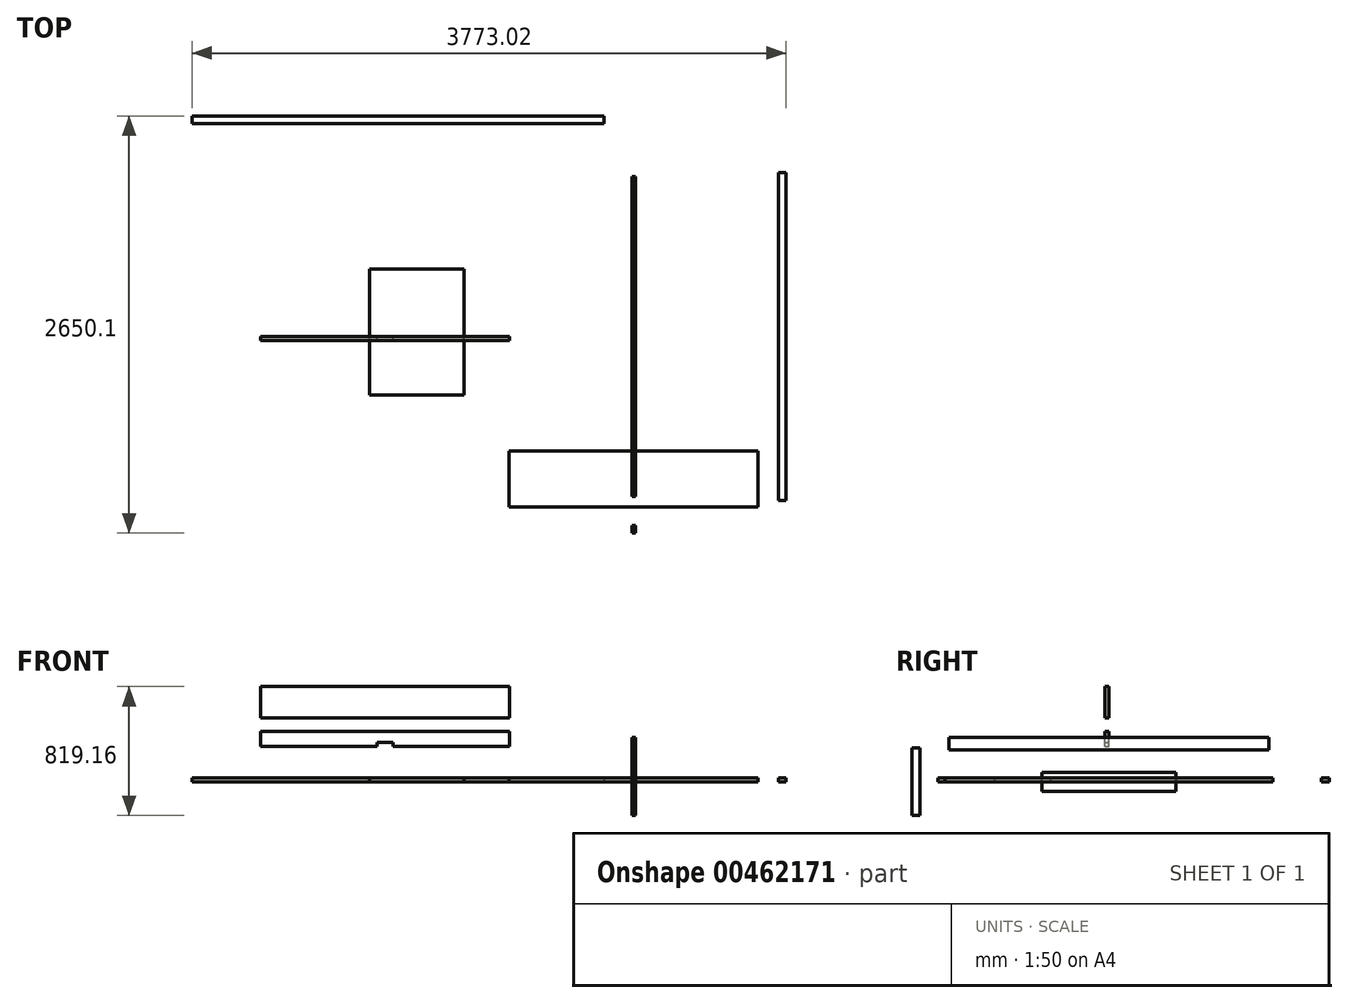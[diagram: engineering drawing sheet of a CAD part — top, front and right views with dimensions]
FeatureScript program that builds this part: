
annotation { "Feature Type Name" : "Feature", "Feature Type Description" : "" }
export const myFeature = defineFeature(function(context is Context, id is Id, definition is map)
    precondition{}
    {
        {
            var Q0;
            Q0=qCreatedBy(makeId("Right.planeOp"),FACE);
            var sketch = newSketch(context, id + "F0", { "sketchPlane" : qUnion([Q0])});
            skLineSegment(sketch, "E0", {"start": v(-1409.76, 0) * mm, "end": v(1225.16, 0) * mm, "construction": true});
            skLineSegment(sketch, "E1.bottom", {"start": v(-1199.58, -215) * mm, "end": v(-1249.58, -215) * mm});
            skLineSegment(sketch, "E1.top", {"start": v(-1199.58, 215) * mm, "end": v(-1249.58, 215) * mm});
            skLineSegment(sketch, "E1.left", {"start": v(-1199.58, -215) * mm, "end": v(-1199.58, 215) * mm});
            skLineSegment(sketch, "E1.right", {"start": v(-1249.58, -215) * mm, "end": v(-1249.58, 215) * mm});
            skPoint(sketch, "E1.middle", {"position": v(-1224.58, 0) * mm});
            skLineSegment(sketch, "E2.bottom", {"start": v(1016.5, 202.42) * mm, "end": v(-1016.5, 202.42) * mm});
            skLineSegment(sketch, "E2.top", {"start": v(1016.5, 282.42) * mm, "end": v(-1016.5, 282.42) * mm});
            skLineSegment(sketch, "E2.left", {"start": v(1016.5, 202.42) * mm, "end": v(1016.5, 282.42) * mm});
            skLineSegment(sketch, "E2.right", {"start": v(-1016.5, 202.42) * mm, "end": v(-1016.5, 282.42) * mm});
            skPoint(sketch, "E2.middle", {"position": v(0, 242.42) * mm});
            skLineSegment(sketch, "E3.bottom", {"start": v(425, -60) * mm, "end": v(-425, -60) * mm});
            skLineSegment(sketch, "E3.top", {"start": v(425, 60) * mm, "end": v(-425, 60) * mm});
            skLineSegment(sketch, "E3.left", {"start": v(425, -60) * mm, "end": v(425, 60) * mm});
            skLineSegment(sketch, "E3.right", {"start": v(-425, -60) * mm, "end": v(-425, 60) * mm});
            skPoint(sketch, "E3.middle", {"position": v(0, 0) * mm});
            skSolve(sketch);
        }
        {
            var Q0;
            Q0 = qSketchRegion(id + "F0", true);
            extrude(context, id + "F1", {"entities" : qUnion([Q0]), "depth" : 25 * mm});
        }
        {
            var Q0;
            Q0=qCreatedBy(makeId("Top.planeOp"),FACE);
            var sketch = newSketch(context, id + "F2", { "sketchPlane" : qUnion([Q0])});
            skLineSegment(sketch, "E4.bottom", {"start": v(800.4, -1084.57) * mm, "end": v(-780.6, -1084.57) * mm});
            skLineSegment(sketch, "E4.top", {"start": v(800.4, -726.57) * mm, "end": v(-780.6, -726.57) * mm});
            skLineSegment(sketch, "E4.left", {"start": v(800.4, -1084.57) * mm, "end": v(800.4, -726.57) * mm});
            skLineSegment(sketch, "E4.right", {"start": v(-780.6, -1084.57) * mm, "end": v(-780.6, -726.57) * mm});
            skPoint(sketch, "E4.middle", {"position": v(9.9, -905.57) * mm});
            skLineSegment(sketch, "E5.bottom", {"start": v(-1065.51, -372.32) * mm, "end": v(-1665.51, -372.32) * mm});
            skLineSegment(sketch, "E5.top", {"start": v(-1065.51, 427.68) * mm, "end": v(-1665.51, 427.68) * mm});
            skLineSegment(sketch, "E5.left", {"start": v(-1065.51, -372.32) * mm, "end": v(-1065.51, 427.68) * mm});
            skLineSegment(sketch, "E5.right", {"start": v(-1665.51, -372.32) * mm, "end": v(-1665.51, 427.68) * mm});
            skPoint(sketch, "E5.middle", {"position": v(-1365.51, 27.68) * mm});
            skSolve(sketch);
        }
        {
            var Q0;
            Q0 = qSketchRegion(id + "F2", true);
            extrude(context, id + "F3", {"entities" : qUnion([Q0]), "depth" : 25 * mm});
        }
        {
            var Q0;
            Q0=qCreatedBy(makeId("Front.planeOp"),FACE);
            var sketch = newSketch(context, id + "F4", { "sketchPlane" : qUnion([Q0])});
            skLineSegment(sketch, "E6.bottom", {"start": v(-777.44, 404.16) * mm, "end": v(-2358.44, 404.16) * mm});
            skLineSegment(sketch, "E6.top", {"start": v(-777.44, 604.16) * mm, "end": v(-2358.44, 604.16) * mm});
            skLineSegment(sketch, "E6.left", {"start": v(-777.44, 404.16) * mm, "end": v(-777.44, 604.16) * mm});
            skLineSegment(sketch, "E6.right", {"start": v(-2358.44, 404.16) * mm, "end": v(-2358.44, 604.16) * mm});
            skPoint(sketch, "E6.middle", {"position": v(-1567.94, 504.16) * mm});
            skLineSegment(sketch, "E7.bottom", {"start": v(-777.44, 225.3) * mm, "end": v(-1516.94, 225.3) * mm});
            skLineSegment(sketch, "E7.top", {"start": v(-777.44, 320.3) * mm, "end": v(-2358.44, 320.3) * mm});
            skLineSegment(sketch, "E7.left", {"start": v(-777.44, 225.3) * mm, "end": v(-777.44, 320.3) * mm});
            skLineSegment(sketch, "E7.right", {"start": v(-2358.44, 225.3) * mm, "end": v(-2358.44, 320.3) * mm});
            skPoint(sketch, "E7.middle", {"position": v(-1567.94, 272.8) * mm});
            skLineSegment(sketch, "E8", {"start": v(-1567.94, 320.3) * mm, "end": v(-1567.94, 225.3) * mm, "construction": true});
            skPoint(sketch, "E9", {"position": v(-1618.94, 225.3) * mm});
            skPoint(sketch, "E10", {"position": v(-1618.94, 251.3) * mm});
            skLineSegment(sketch, "E11", {"start": v(-1618.94, 225.3) * mm, "end": v(-1618.94, 251.3) * mm});
            skLineSegment(sketch, "E12", {"start": v(-1618.94, 251.3) * mm, "end": v(-1567.94, 251.3) * mm});
            skLineSegment(sketch, "E13.MirrorCS", {"start": v(-1516.94, 225.3) * mm, "end": v(-1516.94, 251.3) * mm});
            skLineSegment(sketch, "E14.MirrorCS", {"start": v(-1516.94, 251.3) * mm, "end": v(-1567.94, 251.3) * mm});
            skLineSegment(sketch, "E15.trimOffspring", {"start": v(-1618.94, 225.3) * mm, "end": v(-2358.44, 225.3) * mm});
            skSolve(sketch);
        }
        {
            var Q0;
            Q0 = qSketchRegion(id + "F4", true);
            extrude(context, id + "F5", {"entities" : qUnion([Q0]), "depth" : 25 * mm});
        }
        {
            var Q0;
            Q0=qCreatedBy(makeId("Top.planeOp"),FACE);
            var sketch = newSketch(context, id + "F6", { "sketchPlane" : qUnion([Q0])});
            skLineSegment(sketch, "E16.bottom", {"start": v(980.27, -1041.5) * mm, "end": v(930.27, -1041.5) * mm});
            skLineSegment(sketch, "E16.top", {"start": v(980.27, 1041.5) * mm, "end": v(930.27, 1041.5) * mm});
            skLineSegment(sketch, "E16.left", {"start": v(980.27, -1041.5) * mm, "end": v(980.27, 1041.5) * mm});
            skLineSegment(sketch, "E16.right", {"start": v(930.27, -1041.5) * mm, "end": v(930.27, 1041.5) * mm});
            skPoint(sketch, "E16.middle", {"position": v(955.27, 0) * mm});
            skLineSegment(sketch, "E17.bottom", {"start": v(-177.14, 1350.52) * mm, "end": v(-2792.75, 1350.52) * mm});
            skLineSegment(sketch, "E17.top", {"start": v(-177.14, 1400.52) * mm, "end": v(-2792.75, 1400.52) * mm});
            skLineSegment(sketch, "E17.left", {"start": v(-177.14, 1350.52) * mm, "end": v(-177.14, 1400.52) * mm});
            skLineSegment(sketch, "E17.right", {"start": v(-2792.75, 1350.52) * mm, "end": v(-2792.75, 1400.52) * mm});
            skPoint(sketch, "E17.middle", {"position": v(-1484.95, 1375.52) * mm});
            skSolve(sketch);
        }
        {
            var Q0;
            Q0 = qSketchRegion(id + "F6", true);
            extrude(context, id + "F7", {"entities" : qUnion([Q0]), "depth" : 25 * mm});
        }
    });
